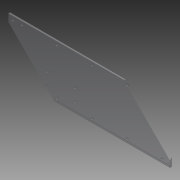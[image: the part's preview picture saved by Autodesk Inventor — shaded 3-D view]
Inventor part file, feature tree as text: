
AUTODESK INVENTOR PART (.ipt)
format: ipt  version: 2014 SP1 (Build 180222100, 222)  size: 102,912 bytes
history: native  units: in
note: dims shown in document units (in); Inventor stores cm internally (conversion verified against a paired STEP export)
features: reference x4, extrude x1, sketch x1
ambient origin geometry x8: Origin, YZ Plane, XZ Plane, XY Plane, X Axis, Y Axis, Z Axis, Center Point
bodies: Solid1 (feature_tree)
feature tree (6):
  extrude  "Extrusion1"  Depth=4.2478in
  sketch  "Sketch1"  dims[d0=13.0in d1=4.2478in d2=0.125in d3=0.0in]
  reference  "Reference1"
  reference  "Reference2"
  reference  "Reference3"
  reference  "Reference4"
